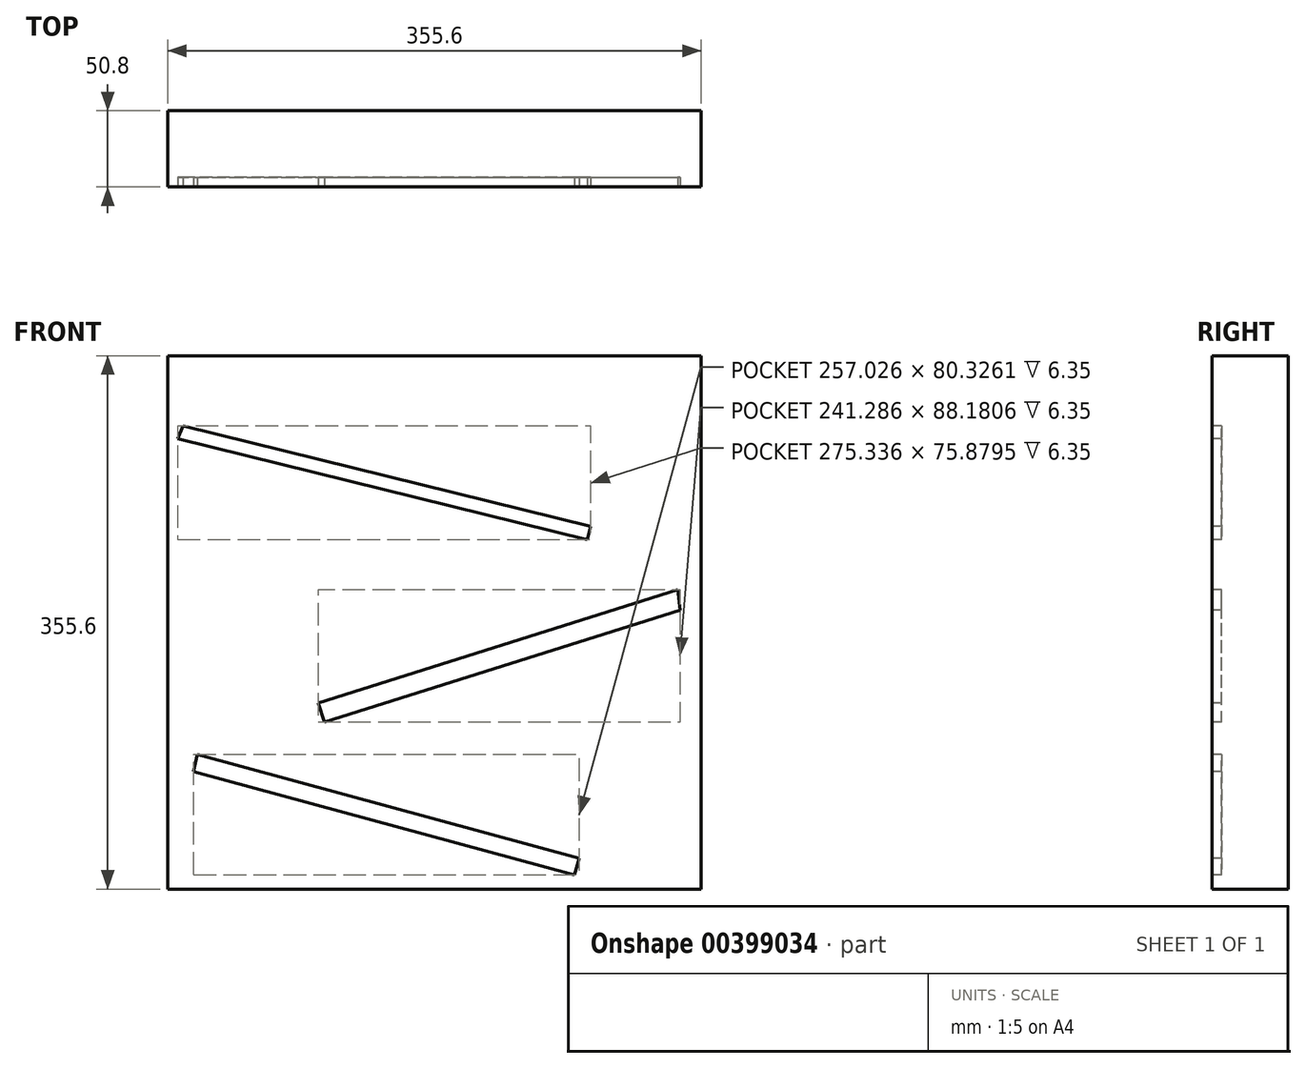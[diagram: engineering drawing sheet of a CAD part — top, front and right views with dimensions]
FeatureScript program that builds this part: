
annotation { "Feature Type Name" : "Feature", "Feature Type Description" : "" }
export const myFeature = defineFeature(function(context is Context, id is Id, definition is map)
    precondition{}
    {
        {
            var Q0;
            Q0=qCreatedBy(makeId("Front.planeOp"),FACE);
            var sketch = newSketch(context, id + "F0", { "sketchPlane" : qUnion([Q0])});
            skLineSegment(sketch, "E0.bottom", {"start": v(177.8, 177.8) * mm, "end": v(-177.8, 177.8) * mm});
            skLineSegment(sketch, "E0.top", {"start": v(177.8, -177.8) * mm, "end": v(-177.8, -177.8) * mm});
            skLineSegment(sketch, "E0.left", {"start": v(177.8, 177.8) * mm, "end": v(177.8, -177.8) * mm});
            skLineSegment(sketch, "E0.right", {"start": v(-177.8, 177.8) * mm, "end": v(-177.8, -177.8) * mm});
            skPoint(sketch, "E0.middle", {"position": v(0, 0) * mm});
            skSolve(sketch);
        }
        {
            var Q0;
            Q0 = qSketchRegion(id + "F0", true);
            extrude(context, id + "F1", {"entities" : qUnion([Q0]), "depth" : 50.8 * mm});
        }
        {
            var Q0;
            Q0=makeQuery(id+"F1.opExtrude","CAP_FACE",FACE,{"disambiguationData":[OSD([sQuery(id+"F0.wireOp",EDGE,"E0.bottom"),sQuery(id+"F0.wireOp",EDGE,"E0.top"),sQuery(id+"F0.wireOp",EDGE,"E0.left"),sQuery(id+"F0.wireOp",EDGE,"E0.right")])],"isStart":false});
            var sketch = newSketch(context, id + "F2", { "sketchPlane" : qUnion([Q0])});
            skLineSegment(sketch, "E1", {"start": v(-171.2, 122.47) * mm, "end": v(101.95, 55.14) * mm});
            skLineSegment(sketch, "E2", {"start": v(101.95, 55.14) * mm, "end": v(104.14, 64.04) * mm});
            skLineSegment(sketch, "E3", {"start": v(104.14, 64.04) * mm, "end": v(-167.6, 131.02) * mm});
            skLineSegment(sketch, "E4", {"start": v(-167.6, 131.02) * mm, "end": v(-171.2, 122.47) * mm});
            skLineSegment(sketch, "E5", {"start": v(-73.4, -66.52) * mm, "end": v(-77.38, -53.87) * mm});
            skLineSegment(sketch, "E6", {"start": v(-77.38, -53.87) * mm, "end": v(162.43, 21.66) * mm});
            skLineSegment(sketch, "E7", {"start": v(-73.4, -66.52) * mm, "end": v(163.9, 8.23) * mm});
            skLineSegment(sketch, "E8", {"start": v(163.9, 8.23) * mm, "end": v(162.43, 21.66) * mm});
            skLineSegment(sketch, "E9", {"start": v(-157.93, -88.09) * mm, "end": v(96.55, -157.1) * mm});
            skLineSegment(sketch, "E10", {"start": v(96.55, -157.1) * mm, "end": v(93.49, -168.42) * mm});
            skLineSegment(sketch, "E11", {"start": v(93.49, -168.42) * mm, "end": v(-160.47, -99.55) * mm});
            skLineSegment(sketch, "E12", {"start": v(-160.47, -99.55) * mm, "end": v(-157.93, -88.09) * mm});
            skSolve(sketch);
        }
        {
            var Q0;
            Q0 = qSketchRegion(id + "F2", true);
            extrude(context, id + "F3", {"entities" : qUnion([Q0]), "operationType" : NewBodyOperationType.REMOVE, "oppositeDirection" : true, "depth" : 6.35 * mm});
        }
        {
            var Q0;
            Q0 = qSketchRegion(id + "F2", true);
            extrude(context, id + "F4", {"entities" : qUnion([Q0]), "operationType" : NewBodyOperationType.REMOVE, "oppositeDirection" : true, "depth" : 6.35 * mm});
        }
    });
